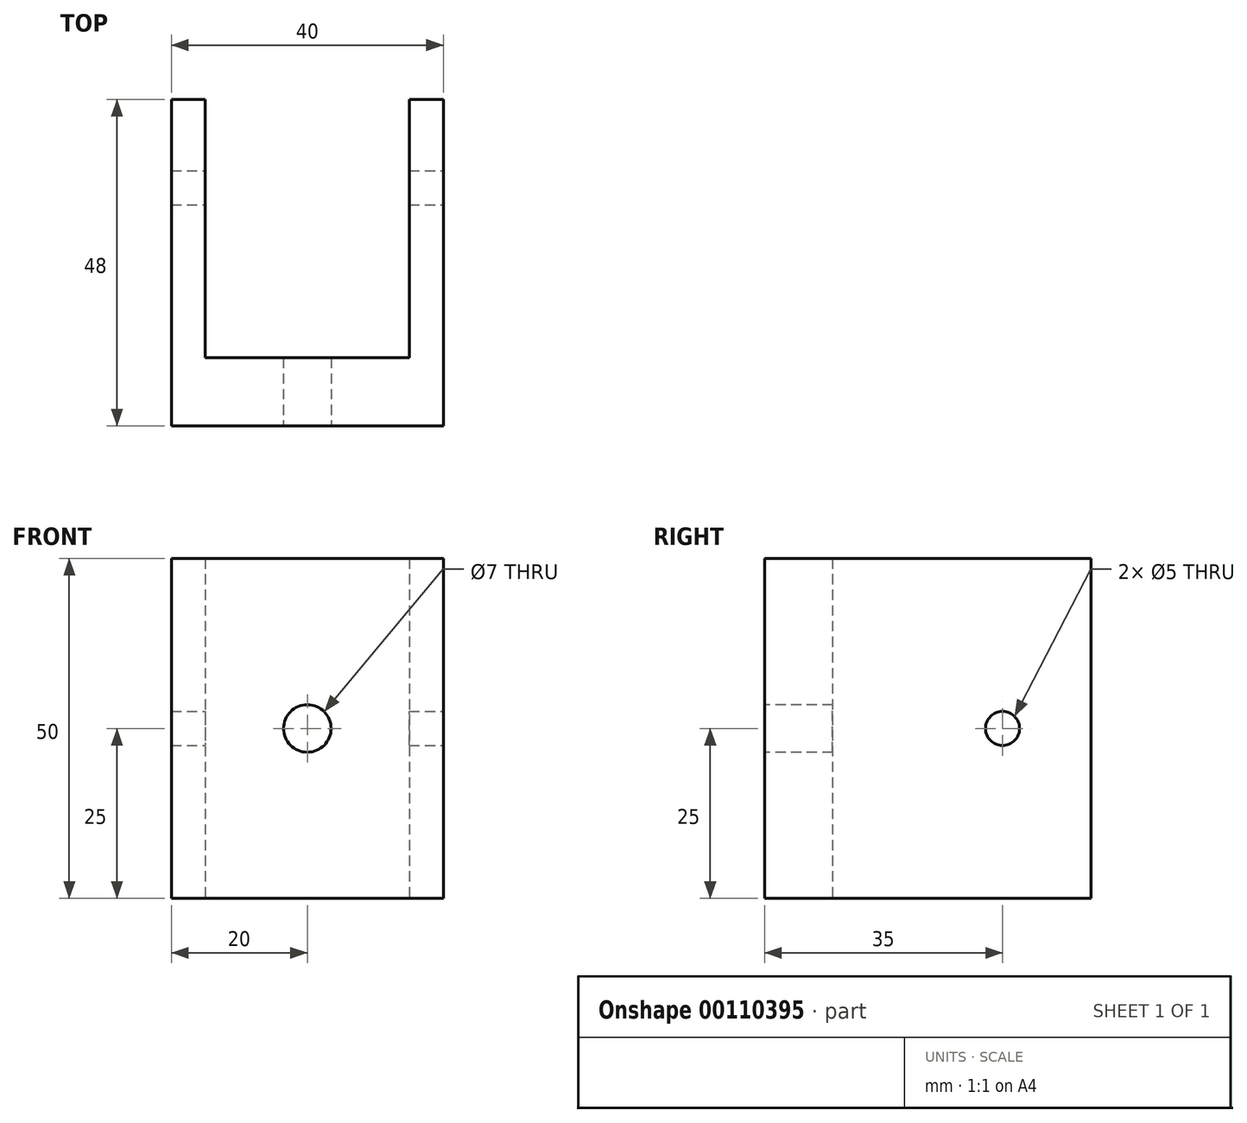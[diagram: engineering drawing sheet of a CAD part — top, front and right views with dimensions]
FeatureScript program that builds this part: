
annotation { "Feature Type Name" : "Feature", "Feature Type Description" : "" }
export const myFeature = defineFeature(function(context is Context, id is Id, definition is map)
    precondition{}
    {
        {
            var Q0;
            Q0=qCreatedBy(makeId("Top.planeOp"),FACE);
            var sketch = newSketch(context, id + "F0", { "sketchPlane" : qUnion([Q0])});
            skLineSegment(sketch, "E0", {"start": v(0, 0) * mm, "end": v(40, 0) * mm});
            skLineSegment(sketch, "E1", {"start": v(40, 0) * mm, "end": v(40, 48) * mm});
            skLineSegment(sketch, "E2", {"start": v(40, 48) * mm, "end": v(35, 48) * mm});
            skLineSegment(sketch, "E3", {"start": v(35, 48) * mm, "end": v(35, 10) * mm});
            skLineSegment(sketch, "E4", {"start": v(35, 10) * mm, "end": v(5, 10) * mm});
            skLineSegment(sketch, "E5", {"start": v(5, 10) * mm, "end": v(5, 48) * mm});
            skLineSegment(sketch, "E6", {"start": v(5, 48) * mm, "end": v(0, 48) * mm});
            skLineSegment(sketch, "E7", {"start": v(0, 48) * mm, "end": v(0, 0) * mm});
            skSolve(sketch);
        }
        {
            var Q0;
            Q0 = qSketchRegion(id + "F0", true);
            extrude(context, id + "F1", {"entities" : qUnion([Q0]), "depth" : 50 * mm, "offsetDistance" : 25 * mm});
        }
        {
            var Q0;
            Q0=makeQuery(id+"F1.opExtrude","SWEPT_FACE",FACE,{"disambiguationData":[OSD([sQuery(id+"F0.wireOp",EDGE,"E0")])]});
            var sketch = newSketch(context, id + "F2", { "sketchPlane" : qUnion([Q0])});
            skCircle(sketch, "E8", {"center": v(20, 25) * mm, "radius": 3.5 * mm});
            skPoint(sketch, "E8.centerSnap0", {"position": v(20, 50) * mm});
            skPoint(sketch, "E8.centerSnap1", {"position": v(40, 25) * mm});
            skSolve(sketch);
        }
        {
            var Q0;
            Q0 = qSketchRegion(id + "F2", true);
            extrude(context, id + "F3", {"entities" : qUnion([Q0]), "operationType" : NewBodyOperationType.REMOVE, "oppositeDirection" : true, "depth" : 25 * mm, "offsetDistance" : 25 * mm});
        }
        {
            var Q0;
            Q0=makeQuery(id+"F1.opExtrude","SWEPT_FACE",FACE,{"disambiguationData":[OSD([sQuery(id+"F0.wireOp",EDGE,"E1")])]});
            var sketch = newSketch(context, id + "F4", { "sketchPlane" : qUnion([Q0])});
            skCircle(sketch, "E9", {"center": v(35, 25) * mm, "radius": 2.5 * mm});
            skPoint(sketch, "E9.centerSnap0", {"position": v(48, 25) * mm});
            skSolve(sketch);
        }
        {
            var Q0;
            Q0 = qSketchRegion(id + "F4", true);
            extrude(context, id + "F5", {"entities" : qUnion([Q0]), "operationType" : NewBodyOperationType.REMOVE, "endBound" : BoundingType.THROUGH_ALL, "oppositeDirection" : true, "depth" : 25 * mm, "offsetDistance" : 25 * mm});
        }
    });
